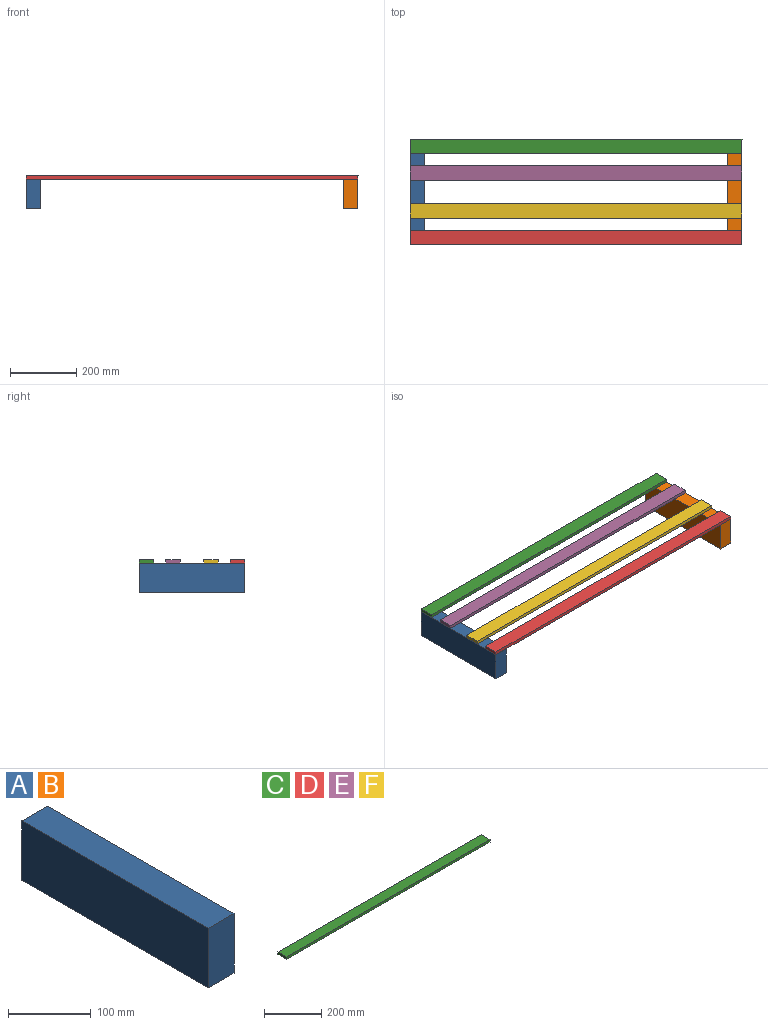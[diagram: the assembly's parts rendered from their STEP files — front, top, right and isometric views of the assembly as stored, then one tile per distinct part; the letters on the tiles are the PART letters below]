
ASSEMBLY  parts=6 mates=3
PART A: 6 faces, bbox 44x318x88 mm
  f0: plane 318x88mm, normal (1,0,0), area 27984mm2, adj f1,f3,f4,f5
  f1: plane 318x44mm, normal (0,0,1), area 13992mm2, adj f0,f2,f4,f5
  f2: plane 318x88mm, normal (-1,0,0), area 27984mm2, adj f1,f3,f4,f5
  f3: plane 318x44mm, normal (0,0,-1), area 13992mm2, adj f0,f2,f4,f5
  f4: plane 88x44mm, normal (0,-1,0), area 3872mm2, adj f0,f1,f2,f3
  f5: plane 88x44mm, normal (0,1,0), area 3872mm2, adj f0,f1,f2,f3
PART B: same geometry as A
PART C: 6 faces, bbox 1000x44x10 mm
  f0: plane 1000x44mm, normal (0,0,-1), area 44000mm2, adj f1,f3,f4,f5
  f1: plane 1000x10mm, normal (0,1,0), area 10000mm2, adj f0,f2,f4,f5
  f2: plane 1000x44mm, normal (0,0,1), area 44000mm2, adj f1,f3,f4,f5
  f3: plane 1000x10mm, normal (0,-1,0), area 10000mm2, adj f0,f2,f4,f5
  f4: plane 44x10mm, normal (1,0,0), area 440mm2, adj f0,f1,f2,f3
  f5: plane 44x10mm, normal (-1,0,0), area 440mm2, adj f0,f1,f2,f3
PART D: same geometry as C
PART E: same geometry as C
PART F: same geometry as C
PLACE A t=(-315.37,166.73,-208.9)mm
PLACE B rot(axis=(0.44,0.88,-0.19),0deg) t=(640.63,166.73,-208.9)mm
PLACE C t=(-337.37,144.73,-159.9)mm
PLACE D t=(-337.37,-129.27,-159.9)mm
PLACE E t=(-337.37,64.73,-159.9)mm
PLACE F t=(-337.37,-49.27,-159.9)mm
MATE fastened B.f1 <-> D.f0  axis (0,0,1) through (662.63,-151.27,-164.9)mm
MATE fastened D.f0 <-> A.f1  axis (0,0,-1) through (-337.37,-151.27,-164.9)mm
MATE fastened C.f0 <-> A.f1  axis (0,0,1) through (-337.37,166.73,-164.9)mm
